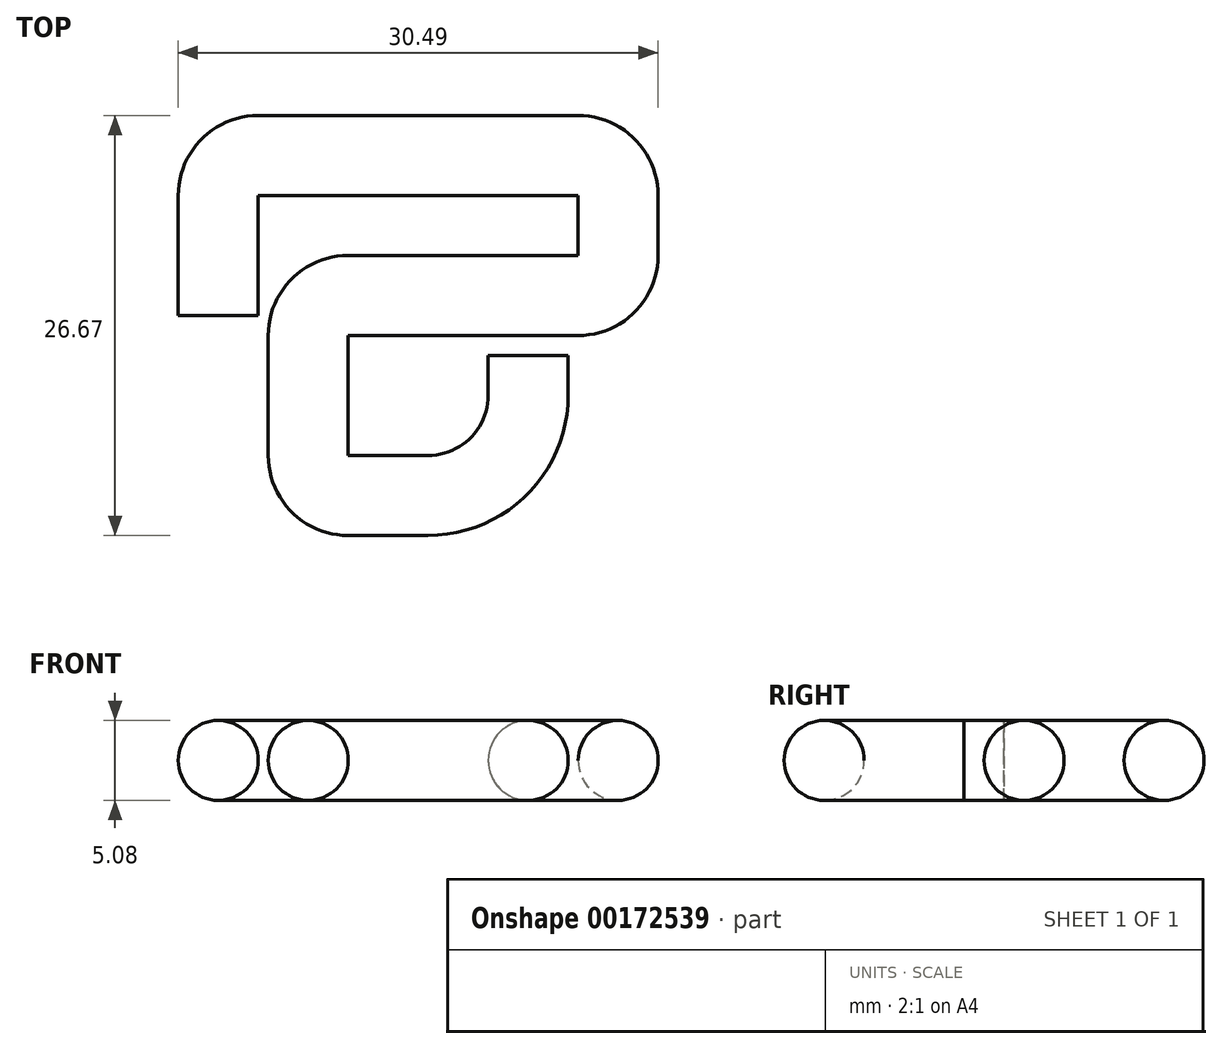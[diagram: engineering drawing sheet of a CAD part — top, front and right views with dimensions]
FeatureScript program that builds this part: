
annotation { "Feature Type Name" : "Feature", "Feature Type Description" : "" }
export const myFeature = defineFeature(function(context is Context, id is Id, definition is map)
    precondition{}
    {
        {
            var Q0;
            Q0=qCreatedBy(makeId("Top.planeOp"),FACE);
            var sketch = newSketch(context, id + "F0", { "sketchPlane" : qUnion([Q0])});
            skLineSegment(sketch, "E0", {"start": v(2.54, 0) * mm, "end": v(7.62, 0) * mm});
            skLineSegment(sketch, "E1", {"start": v(0, 2.54) * mm, "end": v(0, 10.16) * mm});
            skLineSegment(sketch, "E2", {"start": v(2.54, 12.7) * mm, "end": v(17.14, 12.7) * mm});
            skLineSegment(sketch, "E3", {"start": v(19.69, 15.24) * mm, "end": v(19.69, 19.05) * mm});
            skLineSegment(sketch, "E4", {"start": v(17.14, 21.59) * mm, "end": v(-3.18, 21.59) * mm});
            skLineSegment(sketch, "E5", {"start": v(-5.72, 19.05) * mm, "end": v(-5.72, 11.43) * mm});
            skPoint(sketch, "E6.visualSharp", {"position": v(-5.72, 21.59) * mm});
            skArc(sketch, "E6.filletArc", {"start": v(-3.18, 21.59) * mm, "mid": v(-4.97, 20.85) * mm, "end": v(-5.72, 19.05) * mm});
            skPoint(sketch, "E7.visualSharp", {"position": v(19.69, 21.59) * mm});
            skArc(sketch, "E7.filletArc", {"start": v(19.69, 19.05) * mm, "mid": v(18.94, 20.85) * mm, "end": v(17.14, 21.59) * mm});
            skPoint(sketch, "E8.visualSharp", {"position": v(0, 12.7) * mm});
            skArc(sketch, "E8.filletArc", {"start": v(2.54, 12.7) * mm, "mid": v(0.74, 11.96) * mm, "end": v(0, 10.16) * mm});
            skPoint(sketch, "E9.visualSharp", {"position": v(13.97, 0) * mm});
            skPoint(sketch, "E10.visualSharp", {"position": v(19.69, 12.7) * mm});
            skArc(sketch, "E10.filletArc", {"start": v(17.14, 12.7) * mm, "mid": v(18.94, 13.44) * mm, "end": v(19.69, 15.24) * mm});
            skPoint(sketch, "E11.visualSharp", {"position": v(0, 0) * mm});
            skArc(sketch, "E11.filletArc", {"start": v(0, 2.54) * mm, "mid": v(0.74, 0.74) * mm, "end": v(2.54, 0) * mm});
            skLineSegment(sketch, "E12", {"start": v(13.97, 6.35) * mm, "end": v(13.97, 8.9) * mm});
            skArc(sketch, "E13.filletArc", {"start": v(7.62, 0) * mm, "mid": v(12.11, 1.86) * mm, "end": v(13.97, 6.35) * mm});
            skSolve(sketch);
        }
        {
            var Q0;
            Q0=qCreatedBy(makeId("Front.planeOp"),FACE);
            var Q1;
            Q1=sQuery(id+"F0.wireOp",VERTEX,"E5.end");
            cPlane(context, id + "F1", {"entities" : qUnion([Q0, Q1]), "cplaneType" : CPlaneType.PLANE_POINT, "offset" : 50.8 * mm, "width" : 152.4 * mm, "height" : 152.4 * mm});
        }
        {
            var Q0;
            Q0=qCreatedBy(id+"F1.planeOp",FACE);
            var sketch = newSketch(context, id + "F2", { "sketchPlane" : qUnion([Q0])});
            skCircle(sketch, "E14", {"center": v(-5.72, 0) * mm, "radius": 2.54 * mm});
            skSolve(sketch);
        }
        {
            var Q0;
            Q0=makeQuery(id+"F2.imprint","IMPRINT",FACE,{"disambiguationData":[TD([[makeQuery(id+"F2.imprint","IMPRINT",EDGE,{"derivedFrom":sQuery(id+"F2.wireOp",EDGE,"E14")}),1.0]])]});
            var Q1;
            Q1 = qConstructionFilter(qBodyType(qCreatedBy(id + "F0" ,EDGE), BodyType.WIRE), ConstructionObject.NO);
            sweep(context, id + "F3", {"profiles" : qUnion([Q0]), "path" : qUnion([Q1])});
        }
    });
